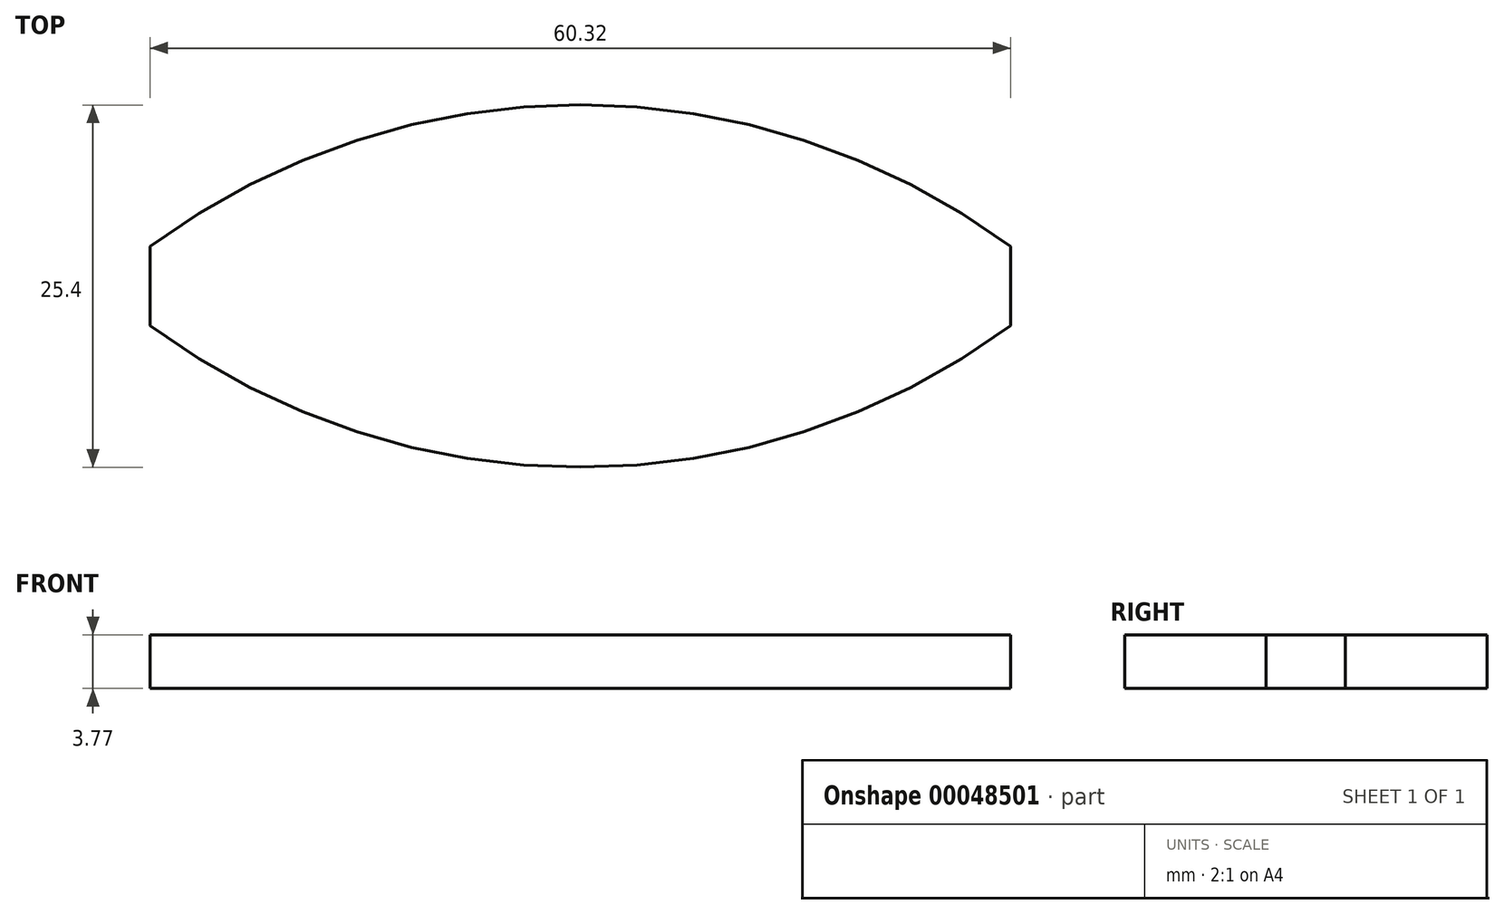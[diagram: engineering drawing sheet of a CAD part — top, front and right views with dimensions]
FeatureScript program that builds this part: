
annotation { "Feature Type Name" : "Feature", "Feature Type Description" : "" }
export const myFeature = defineFeature(function(context is Context, id is Id, definition is map)
    precondition{}
    {
        {
            var Q0;
            Q0=qCreatedBy(makeId("Top.planeOp"),FACE);
            var sketch = newSketch(context, id + "F0", { "sketchPlane" : qUnion([Q0])});
            skLineSegment(sketch, "E0.bottom", {"start": v(-30.16, 12.7) * mm, "end": v(30.16, 12.7) * mm, "construction": true});
            skLineSegment(sketch, "E0.top", {"start": v(-30.16, -12.7) * mm, "end": v(30.16, -12.7) * mm, "construction": true});
            skLineSegment(sketch, "E0.left", {"start": v(-30.16, 12.7) * mm, "end": v(-30.16, -12.7) * mm, "construction": true});
            skLineSegment(sketch, "E0.right", {"start": v(30.16, 12.7) * mm, "end": v(30.16, -12.7) * mm, "construction": true});
            skLineSegment(sketch, "E1", {"start": v(0, 0) * mm, "end": v(0, -38.1) * mm, "construction": true});
            skPoint(sketch, "E1.endSnap0", {"position": v(0, -12.7) * mm});
            skLineSegment(sketch, "E2", {"start": v(-30.16, 0) * mm, "end": v(30.16, 0) * mm, "construction": true});
            skCircle(sketch, "E3", {"center": v(0, -38.1) * mm, "radius": 50.8 * mm});
            skLineSegment(sketch, "E4", {"start": v(0, 0) * mm, "end": v(0, 38.1) * mm, "construction": true});
            skCircle(sketch, "E5", {"center": v(0, 38.1) * mm, "radius": 50.8 * mm});
            skLineSegment(sketch, "E6", {"start": v(-30.16, 2.78) * mm, "end": v(-30.16, -2.78) * mm});
            skLineSegment(sketch, "E7", {"start": v(30.16, 2.78) * mm, "end": v(30.16, -2.78) * mm});
            skSolve(sketch);
        }
        {
            var Q0;
            {var subQ0=sQuery(id+"F0.wireOp",EDGE,"E6");Q0=makeQuery(id+"F0.imprint","IMPRINT",FACE,{"disambiguationData":[TD([[makeQuery(id+"F0.imprint","IMPRINT",EDGE,{"derivedFrom":subQ0}),1.0]])]});}
            extrude(context, id + "F1", {"entities" : qUnion([Q0]), "depth" : 3.77 * mm});
        }
    });
